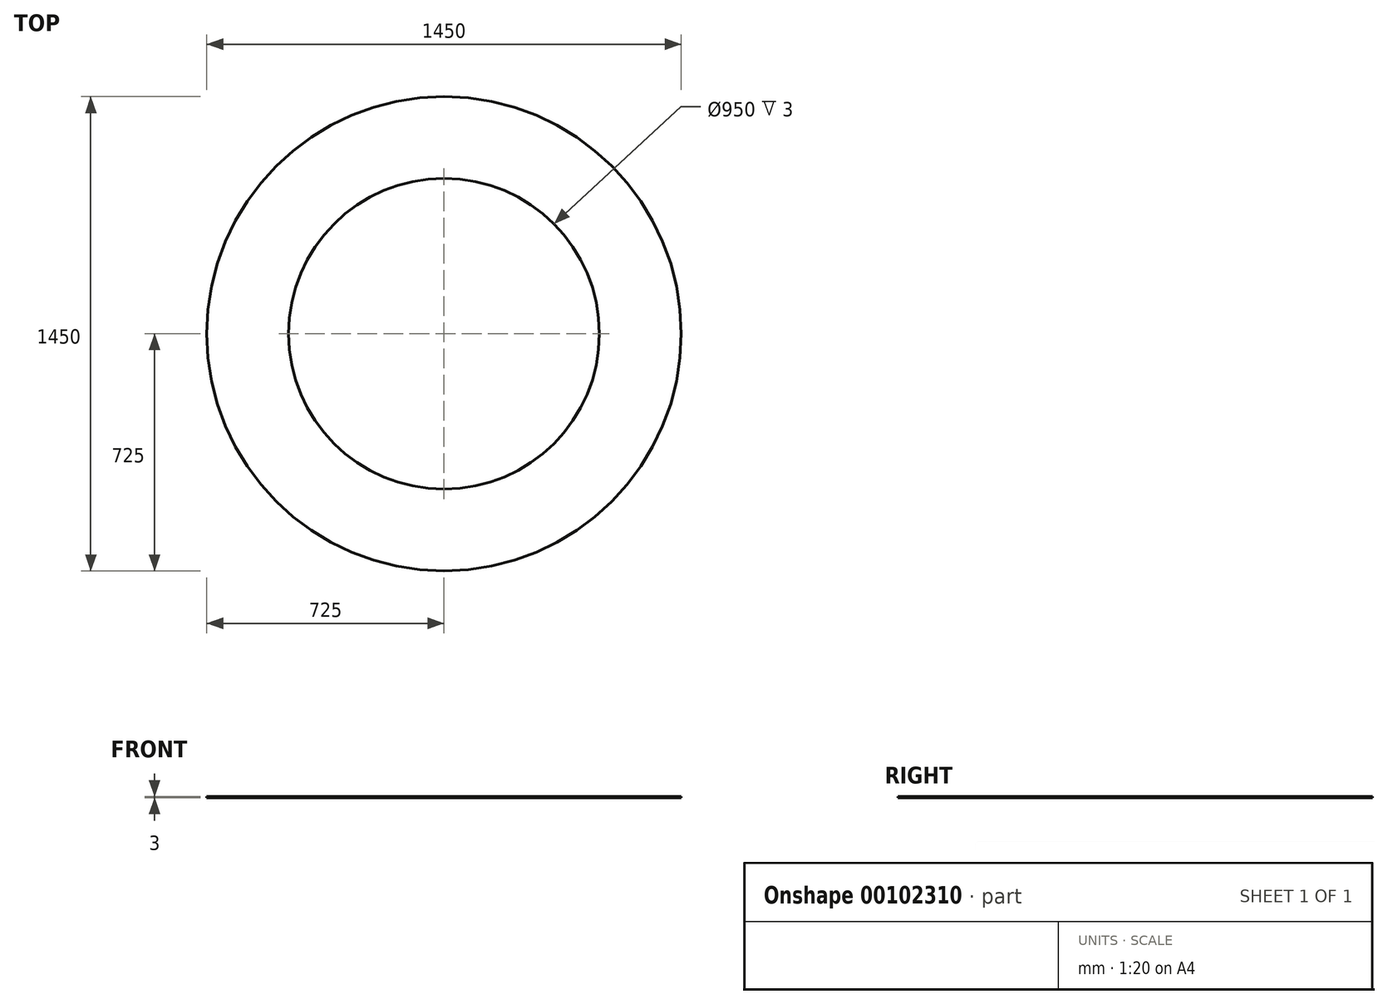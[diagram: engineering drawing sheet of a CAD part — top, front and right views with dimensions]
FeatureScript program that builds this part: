
annotation { "Feature Type Name" : "Feature", "Feature Type Description" : "" }
export const myFeature = defineFeature(function(context is Context, id is Id, definition is map)
    precondition{}
    {
        {
            var Q0;
            Q0=qCreatedBy(makeId("Top.planeOp"),FACE);
            var sketch = newSketch(context, id + "F0", { "sketchPlane" : qUnion([Q0])});
            skCircle(sketch, "E0", {"center": v(0, 0) * mm, "radius": 475 * mm});
            skCircle(sketch, "E1", {"center": v(0, 0) * mm, "radius": 725 * mm});
            skCircle(sketch, "E2", {"center": v(0, 0) * mm, "radius": 650 * mm, "construction": true});
            skSolve(sketch);
        }
        {
            var Q0;
            Q0=makeQuery(id+"F0.imprint","IMPRINT",FACE,{"disambiguationData":[TD([[makeQuery(id+"F0.imprint","IMPRINT",EDGE,{"derivedFrom":sQuery(id+"F0.wireOp",EDGE,"E0")}),-1.0]])]});
            extrude(context, id + "F1", {"entities" : qUnion([Q0]), "depth" : 3 * mm});
        }
    });
